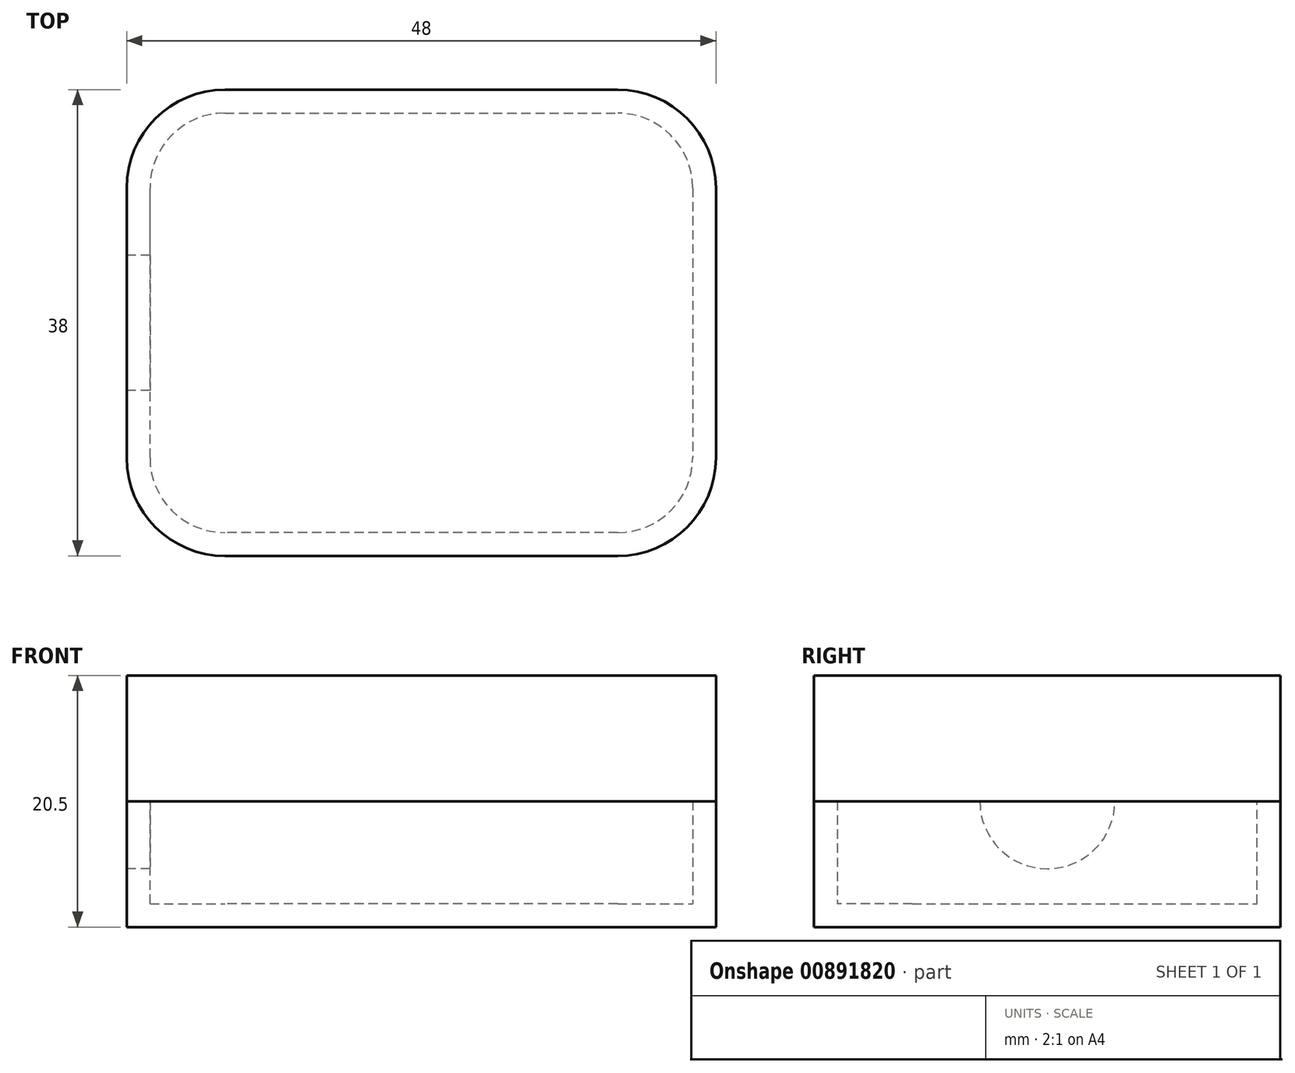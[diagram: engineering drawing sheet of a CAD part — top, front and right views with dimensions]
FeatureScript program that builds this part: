
annotation { "Feature Type Name" : "Feature", "Feature Type Description" : "" }
export const myFeature = defineFeature(function(context is Context, id is Id, definition is map)
    precondition{}
    {
        {
            var Q0;
            Q0=qCreatedBy(makeId("Top.planeOp"),FACE);
            var sketch = newSketch(context, id + "F0", { "sketchPlane" : qUnion([Q0])});
            skLineSegment(sketch, "E0", {"start": v(0, 0) * mm, "end": v(0, 19) * mm});
            skLineSegment(sketch, "E1", {"start": v(0, 19) * mm, "end": v(48, 19) * mm});
            skLineSegment(sketch, "E2", {"start": v(48, 19) * mm, "end": v(48, -19) * mm});
            skLineSegment(sketch, "E3", {"start": v(48, -19) * mm, "end": v(0, -19) * mm});
            skLineSegment(sketch, "E4", {"start": v(0, -19) * mm, "end": v(0, 0) * mm});
            skSolve(sketch);
        }
        {
            var Q0;
            Q0=makeQuery(id+"F0.imprint","IMPRINT",FACE,{"disambiguationData":[TD([[makeQuery(id+"F0.imprint","IMPRINT",EDGE,{"derivedFrom":sQuery(id+"F0.wireOp",EDGE,"E0")}),-1.0]])]});
            extrude(context, id + "F1", {"entities" : qUnion([Q0]), "depth" : 10.25 * mm, "offsetDistance" : 25 * mm});
        }
        {
            var Q0;
            Q0=makeQuery(id+"F1.opExtrude","SWEPT_EDGE",EDGE,{"disambiguationData":[OSD([sQuery(id+"F0.wireOp",EDGE,"E2"),sQuery(id+"F0.wireOp",EDGE,"E3")])]});
            var Q1;
            Q1=makeQuery(id+"F1.opExtrude","SWEPT_EDGE",EDGE,{"disambiguationData":[OSD([sQuery(id+"F0.wireOp",EDGE,"E1"),sQuery(id+"F0.wireOp",EDGE,"E2")])]});
            fillet(context, id + "F2", {"entities" : qUnion([Q0, Q1]), "radius" : 8 * mm, "tangentPropagation" : true, "allowEdgeOverflow" : false});
        }
        {
            var Q0;
            Q0=makeQuery(id+"F1.opExtrude","SWEPT_EDGE",EDGE,{"disambiguationData":[OSD([sQuery(id+"F0.wireOp",EDGE,"E3"),sQuery(id+"F0.wireOp",EDGE,"E4")])]});
            var Q1;
            Q1=makeQuery(id+"F1.opExtrude","SWEPT_EDGE",EDGE,{"disambiguationData":[OSD([sQuery(id+"F0.wireOp",EDGE,"E0"),sQuery(id+"F0.wireOp",EDGE,"E1")])]});
            fillet(context, id + "F3", {"entities" : qUnion([Q0, Q1]), "radius" : 8 * mm, "tangentPropagation" : true, "allowEdgeOverflow" : false});
        }
        {
            var Q0;
            Q0=makeQuery(id+"F1.opExtrude","CAP_FACE",FACE,{"disambiguationData":[OSD([sQuery(id+"F0.wireOp",EDGE,"E0"),sQuery(id+"F0.wireOp",EDGE,"E1"),sQuery(id+"F0.wireOp",EDGE,"E2"),sQuery(id+"F0.wireOp",EDGE,"E3"),sQuery(id+"F0.wireOp",EDGE,"E4")])],"isStart":false});
            shell(context, id + "F4", {"entities" : qUnion([Q0]), "thickness" : 1.9 * mm});
        }
        {
            var Q0;
            Q0=makeQuery(id+"F1.opExtrude","SWEPT_FACE",FACE,{"disambiguationData":[OSD([sQuery(id+"F0.wireOp",EDGE,"E0"),sQuery(id+"F0.wireOp",EDGE,"E4")])]});
            var sketch = newSketch(context, id + "F5", { "sketchPlane" : qUnion([Q0])});
            skCircle(sketch, "E5", {"center": v(0, 10.25) * mm, "radius": 5.5 * mm});
            skSolve(sketch);
        }
        {
            var Q0;
            Q0=makeQuery(id+"F1.opExtrude","CAP_FACE",FACE,{"disambiguationData":[OSD([sQuery(id+"F0.wireOp",EDGE,"E0"),sQuery(id+"F0.wireOp",EDGE,"E1"),sQuery(id+"F0.wireOp",EDGE,"E2"),sQuery(id+"F0.wireOp",EDGE,"E3"),sQuery(id+"F0.wireOp",EDGE,"E4")])],"isStart":false});
            var sketch = newSketch(context, id + "F6", { "sketchPlane" : qUnion([Q0])});
            skArc(sketch, "E6.0", {"start": v(0, -11) * mm, "mid": v(2.34, -16.66) * mm, "end": v(8, -19) * mm});
            skLineSegment(sketch, "E7.0", {"start": v(0, -11) * mm, "end": v(0, 11) * mm});
            skArc(sketch, "E8.0", {"start": v(8, 19) * mm, "mid": v(2.34, 16.66) * mm, "end": v(0, 11) * mm});
            skLineSegment(sketch, "E9.0", {"start": v(8, 19) * mm, "end": v(40, 19) * mm});
            skPoint(sketch, "E10.0", {"position": v(45.66, 16.66) * mm});
            skArc(sketch, "E11.0", {"start": v(48, 11) * mm, "mid": v(45.66, 16.66) * mm, "end": v(40, 19) * mm});
            skLineSegment(sketch, "E12.0", {"start": v(48, 11) * mm, "end": v(48, -11) * mm});
            skArc(sketch, "E13.0", {"start": v(40, -19) * mm, "mid": v(45.66, -16.66) * mm, "end": v(48, -11) * mm});
            skLineSegment(sketch, "E14.0", {"start": v(40, -19) * mm, "end": v(8, -19) * mm});
            skSolve(sketch);
        }
        {
            var Q0;
            Q0 = qSketchRegion(id + "F6", true);
            extrude(context, id + "F7", {"entities" : qUnion([Q0]), "depth" : 10.25 * mm, "offsetDistance" : 25 * mm});
        }
        {
            var Q0;
            {var subQ0=sQuery(id+"F5.wireOp",EDGE,"E5");var subQ1=makeQuery(id+"F1.opExtrude","CAP_EDGE",EDGE,{"disambiguationData":[OSD([sQuery(id+"F0.wireOp",EDGE,"E0"),sQuery(id+"F0.wireOp",EDGE,"E4")])],"isStart":false});var subQ2=makeQuery(id+"F5.imprint","INTERSECT",VERTEX,{"disambiguationData":[OD(0.0)],"derivedFrom":[subQ1,subQ0]});Q0=makeQuery(id+"F5.imprint","IMPRINT",FACE,{"disambiguationData":[TD([[makeQuery(id+"F5.imprint","IMPRINT",EDGE,{"disambiguationData":[TD([[subQ2,-1.0]])],"derivedFrom":subQ0}),1.0]])]});}
            var Q1;
            Q1=makeQuery(id+"F4.opShell","OFFSET_FACE",FACE,{"disambiguationData":[OSD([sQuery(id+"F0.wireOp",EDGE,"E0"),sQuery(id+"F0.wireOp",EDGE,"E4")])]});
            extrude(context, id + "F8", {"entities" : qUnion([Q0]), "operationType" : NewBodyOperationType.REMOVE, "endBound" : BoundingType.UP_TO_SURFACE, "oppositeDirection" : true, "depth" : 25 * mm, "endBoundEntityFace" : qUnion([Q1]), "offsetDistance" : 25 * mm});
        }
    });
